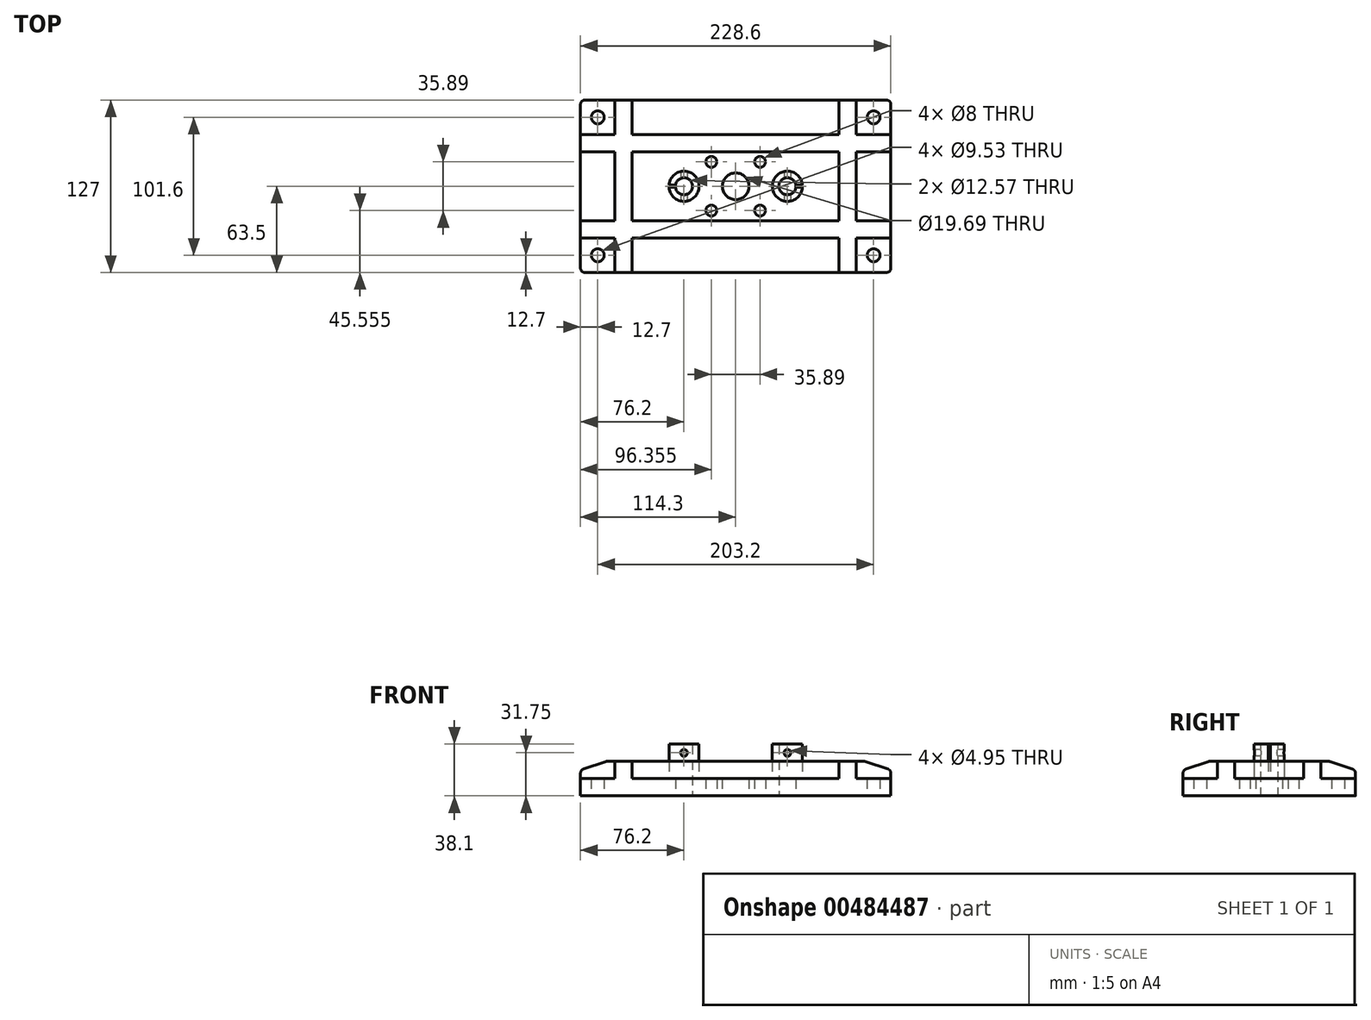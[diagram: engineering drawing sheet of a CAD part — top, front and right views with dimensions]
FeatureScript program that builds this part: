
annotation { "Feature Type Name" : "Feature", "Feature Type Description" : "" }
export const myFeature = defineFeature(function(context is Context, id is Id, definition is map)
    precondition{}
    {
        {
            var Q0;
            Q0=qCreatedBy(makeId("Top.planeOp"),FACE);
            var sketch = newSketch(context, id + "F0", { "sketchPlane" : qUnion([Q0])});
            skCircle(sketch, "E0", {"center": v(0, 0) * mm, "radius": 9.84 * mm});
            skCircle(sketch, "E1", {"center": v(38.1, 0) * mm, "radius": 6.29 * mm});
            skCircle(sketch, "E2", {"center": v(-38.1, 0) * mm, "radius": 6.29 * mm});
            skLineSegment(sketch, "E3", {"start": v(-38.1, 0) * mm, "end": v(0, 0) * mm, "construction": true});
            skLineSegment(sketch, "E4", {"start": v(38.1, 0) * mm, "end": v(0, 0) * mm, "construction": true});
            skLineSegment(sketch, "E5.bottom", {"start": v(-114.3, 63.5) * mm, "end": v(114.3, 63.5) * mm});
            skLineSegment(sketch, "E5.top", {"start": v(-114.3, -63.5) * mm, "end": v(114.3, -63.5) * mm});
            skLineSegment(sketch, "E5.left", {"start": v(-114.3, 63.5) * mm, "end": v(-114.3, -63.5) * mm});
            skLineSegment(sketch, "E5.right", {"start": v(114.3, 63.5) * mm, "end": v(114.3, -63.5) * mm});
            skLineSegment(sketch, "E6.bottom", {"start": v(17.95, 17.95) * mm, "end": v(-17.95, 17.95) * mm, "construction": true});
            skLineSegment(sketch, "E6.top", {"start": v(17.95, -17.95) * mm, "end": v(-17.95, -17.95) * mm, "construction": true});
            skLineSegment(sketch, "E6.left", {"start": v(17.95, 17.95) * mm, "end": v(17.95, -17.95) * mm, "construction": true});
            skLineSegment(sketch, "E6.right", {"start": v(-17.95, 17.95) * mm, "end": v(-17.95, -17.95) * mm, "construction": true});
            skCircle(sketch, "E7", {"center": v(-17.95, 17.95) * mm, "radius": 4 * mm});
            skCircle(sketch, "E8", {"center": v(17.95, 17.95) * mm, "radius": 4 * mm});
            skCircle(sketch, "E9", {"center": v(17.95, -17.95) * mm, "radius": 4 * mm});
            skCircle(sketch, "E10", {"center": v(-17.95, -17.95) * mm, "radius": 4 * mm});
            skLineSegment(sketch, "E11.bottom", {"start": v(-101.6, 50.8) * mm, "end": v(101.6, 50.8) * mm, "construction": true});
            skLineSegment(sketch, "E11.top", {"start": v(-101.6, -50.8) * mm, "end": v(101.6, -50.8) * mm, "construction": true});
            skLineSegment(sketch, "E11.left", {"start": v(-101.6, 50.8) * mm, "end": v(-101.6, -50.8) * mm, "construction": true});
            skLineSegment(sketch, "E11.right", {"start": v(101.6, 50.8) * mm, "end": v(101.6, -50.8) * mm, "construction": true});
            skCircle(sketch, "E12", {"center": v(-101.6, 50.8) * mm, "radius": 4.76 * mm});
            skCircle(sketch, "E13", {"center": v(101.6, 50.8) * mm, "radius": 4.76 * mm});
            skCircle(sketch, "E14", {"center": v(101.6, -50.8) * mm, "radius": 4.76 * mm});
            skCircle(sketch, "E15", {"center": v(-101.6, -50.8) * mm, "radius": 4.76 * mm});
            skSolve(sketch);
        }
        {
            var Q0;
            Q0 = qSketchRegion(id + "F0", true);
            extrude(context, id + "F1", {"entities" : qUnion([Q0]), "depth" : 12.7 * mm});
        }
        {
            var Q0;
            Q0=makeQuery(id+"F1.opExtrude","CAP_FACE",FACE,{"disambiguationData":[OSD([sQuery(id+"F0.wireOp",EDGE,"E0"),sQuery(id+"F0.wireOp",EDGE,"E1"),sQuery(id+"F0.wireOp",EDGE,"E2"),sQuery(id+"F0.wireOp",EDGE,"E5.bottom"),sQuery(id+"F0.wireOp",EDGE,"E5.top"),sQuery(id+"F0.wireOp",EDGE,"E5.left"),sQuery(id+"F0.wireOp",EDGE,"E5.right"),sQuery(id+"F0.wireOp",EDGE,"E7"),sQuery(id+"F0.wireOp",EDGE,"E8"),sQuery(id+"F0.wireOp",EDGE,"E9"),sQuery(id+"F0.wireOp",EDGE,"E10")])],"isStart":false});
            var sketch = newSketch(context, id + "F2", { "sketchPlane" : qUnion([Q0])});
            skCircle(sketch, "E16", {"center": v(-38.1, 0) * mm, "radius": 11.11 * mm});
            skCircle(sketch, "E17", {"center": v(38.1, 0) * mm, "radius": 11.11 * mm});
            skCircle(sketch, "E18.0", {"center": v(-38.1, 0) * mm, "radius": 6.29 * mm});
            skCircle(sketch, "E19.0", {"center": v(38.1, 0) * mm, "radius": 6.29 * mm});
            skSolve(sketch);
        }
        {
            var Q0;
            Q0 = qSketchRegion(id + "F2", true);
            extrude(context, id + "F3", {"entities" : qUnion([Q0]), "operationType" : NewBodyOperationType.ADD, "depth" : 25.4 * mm});
        }
        {
            var Q0;
            Q0=makeQuery(id+"F3.opExtrude","CAP_FACE",FACE,{"disambiguationData":[OSD([sQuery(id+"F2.wireOp",EDGE,"E16"),sQuery(id+"F2.wireOp",EDGE,"E18.0")])],"isStart":false});
            var sketch = newSketch(context, id + "F4", { "sketchPlane" : qUnion([Q0])});
            skLineSegment(sketch, "E20.bottom", {"start": v(-37.57, 0.8) * mm, "end": v(-60.85, 0.8) * mm});
            skLineSegment(sketch, "E20.top", {"start": v(-37.57, -0.8) * mm, "end": v(-60.85, -0.8) * mm});
            skLineSegment(sketch, "E20.left", {"start": v(-37.57, 0.8) * mm, "end": v(-37.57, -0.8) * mm});
            skLineSegment(sketch, "E20.right", {"start": v(-60.85, 0.8) * mm, "end": v(-60.85, -0.8) * mm});
            skPoint(sketch, "E20.middle", {"position": v(-49.21, 0) * mm});
            skLineSegment(sketch, "E21.bottom", {"start": v(42.1, 0.8) * mm, "end": v(65.37, 0.8) * mm});
            skLineSegment(sketch, "E21.top", {"start": v(42.1, -0.8) * mm, "end": v(65.37, -0.8) * mm});
            skLineSegment(sketch, "E21.left", {"start": v(42.1, 0.8) * mm, "end": v(42.1, -0.8) * mm});
            skLineSegment(sketch, "E21.right", {"start": v(65.37, 0.8) * mm, "end": v(65.37, -0.8) * mm});
            skPoint(sketch, "E21.middle", {"position": v(53.73, 0) * mm});
            skSolve(sketch);
        }
        {
            var Q0;
            Q0=makeQuery(id+"F4.imprint","IMPRINT",FACE,{"disambiguationData":[TD([[makeQuery(id+"F4.imprint","IMPRINT",EDGE,{"derivedFrom":sQuery(id+"F4.wireOp",EDGE,"E21.bottom")}),-1.0]])]});
            var Q1;
            {var subQ0=sQuery(id+"F4.wireOp",EDGE,"E20.left");Q1=makeQuery(id+"F4.imprint","IMPRINT",FACE,{"disambiguationData":[TD([[makeQuery(id+"F4.imprint","IMPRINT",EDGE,{"derivedFrom":subQ0}),-1.0]])]});}
            var Q2;
            {var subQ0=sQuery(id+"F4.wireOp",EDGE,"E20.bottom");var subQ1=makeQuery(id+"F3.opExtrude","CAP_EDGE",EDGE,{"disambiguationData":[OSD([sQuery(id+"F2.wireOp",EDGE,"E16")])],"isStart":false});var subQ2=makeQuery(id+"F4.imprint","INTERSECT",VERTEX,{"derivedFrom":[subQ1,subQ0]});Q2=makeQuery(id+"F4.imprint","IMPRINT",FACE,{"disambiguationData":[TD([[makeQuery(id+"F4.imprint","IMPRINT",EDGE,{"disambiguationData":[TD([[subQ2,1.0]])],"derivedFrom":subQ0}),1.0]])]});}
            var Q3;
            {var subQ0=sQuery(id+"F4.wireOp",EDGE,"E20.right");Q3=makeQuery(id+"F4.imprint","IMPRINT",FACE,{"disambiguationData":[TD([[makeQuery(id+"F4.imprint","IMPRINT",EDGE,{"derivedFrom":subQ0}),1.0]])]});}
            var Q4;
            Q4=makeQuery(id+"F1.opExtrude","CAP_FACE",FACE,{"disambiguationData":[OSD([sQuery(id+"F0.wireOp",EDGE,"E0"),sQuery(id+"F0.wireOp",EDGE,"E1"),sQuery(id+"F0.wireOp",EDGE,"E2"),sQuery(id+"F0.wireOp",EDGE,"E5.bottom"),sQuery(id+"F0.wireOp",EDGE,"E5.top"),sQuery(id+"F0.wireOp",EDGE,"E5.left"),sQuery(id+"F0.wireOp",EDGE,"E5.right"),sQuery(id+"F0.wireOp",EDGE,"E7"),sQuery(id+"F0.wireOp",EDGE,"E8"),sQuery(id+"F0.wireOp",EDGE,"E9"),sQuery(id+"F0.wireOp",EDGE,"E10"),sQuery(id+"F0.wireOp",EDGE,"E12"),sQuery(id+"F0.wireOp",EDGE,"E13"),sQuery(id+"F0.wireOp",EDGE,"E14"),sQuery(id+"F0.wireOp",EDGE,"E15")])],"isStart":false});
            extrude(context, id + "F5", {"entities" : qUnion([Q0, Q1, Q2, Q3]), "operationType" : NewBodyOperationType.REMOVE, "endBound" : BoundingType.UP_TO_SURFACE, "oppositeDirection" : true, "endBoundEntityFace" : qUnion([Q4]), "depth" : 25.4 * mm});
        }
        {
            var Q0;
            {var subQ0=sQuery(id+"F0.wireOp",EDGE,"E15");var subQ1=sQuery(id+"F0.wireOp",EDGE,"E14");var subQ2=sQuery(id+"F0.wireOp",EDGE,"E13");var subQ3=sQuery(id+"F0.wireOp",EDGE,"E12");var subQ4=sQuery(id+"F0.wireOp",EDGE,"E10");var subQ5=sQuery(id+"F0.wireOp",EDGE,"E9");var subQ6=sQuery(id+"F0.wireOp",EDGE,"E8");var subQ7=sQuery(id+"F0.wireOp",EDGE,"E7");var subQ8=sQuery(id+"F0.wireOp",EDGE,"E5.right");var subQ9=sQuery(id+"F0.wireOp",EDGE,"E5.left");var subQ10=sQuery(id+"F0.wireOp",EDGE,"E5.top");var subQ11=sQuery(id+"F0.wireOp",EDGE,"E5.bottom");var subQ12=sQuery(id+"F0.wireOp",EDGE,"E2");var subQ13=sQuery(id+"F0.wireOp",EDGE,"E1");var subQ14=sQuery(id+"F0.wireOp",EDGE,"E0");var subQ15=sQuery(id+"F4.wireOp",EDGE,"E20.bottom");Q0=makeQuery(id+"F5.boolean.opBoolean","MERGE",FACE,{"derivedFrom":[makeQuery(id+"F1.opExtrude","CAP_FACE",FACE,{"disambiguationData":[OSD([subQ14,subQ13,subQ12,subQ11,subQ10,subQ9,subQ8,subQ7,subQ6,subQ5,subQ4,subQ3,subQ2,subQ1,subQ0])],"isStart":false}),makeQuery(id+"F5.opExtrude","CAP_FACE",FACE,{"disambiguationData":[OSD([subQ14,subQ13,subQ12,subQ11,subQ10,subQ9,subQ8,subQ7,subQ6,subQ5,subQ4,subQ3,subQ2,subQ1,subQ0]),ownerDisambiguation([makeQuery(id+"F4.imprint","IMPRINT",EDGE,{"disambiguationData":[TD([[makeQuery(id+"F4.imprint","INTERSECT",VERTEX,{"derivedFrom":[subQ15,sQuery(id+"F4.wireOp",EDGE,"E20.left")]}),-1.0]])],"derivedFrom":subQ15})])],"isStart":false}),makeQuery(id+"F5.opExtrude","CAP_FACE",FACE,{"disambiguationData":[OSD([subQ14,subQ13,subQ12,subQ11,subQ10,subQ9,subQ8,subQ7,subQ6,subQ5,subQ4,subQ3,subQ2,subQ1,subQ0]),ownerDisambiguation([makeQuery(id+"F4.imprint","IMPRINT",EDGE,{"derivedFrom":sQuery(id+"F4.wireOp",EDGE,"E21.bottom")})])],"isStart":false})]});}
            var sketch = newSketch(context, id + "F6", { "sketchPlane" : qUnion([Q0])});
            skLineSegment(sketch, "E22.bottom", {"start": v(-88.9, 63.5) * mm, "end": v(-76.2, 63.5) * mm});
            skLineSegment(sketch, "E22.top", {"start": v(-88.9, -63.5) * mm, "end": v(-76.2, -63.5) * mm});
            skLineSegment(sketch, "E22.left", {"start": v(-88.9, 63.5) * mm, "end": v(-88.9, -63.5) * mm});
            skLineSegment(sketch, "E22.right", {"start": v(-76.2, 63.5) * mm, "end": v(-76.2, -63.5) * mm});
            skLineSegment(sketch, "E23.bottom", {"start": v(88.9, 63.5) * mm, "end": v(76.2, 63.5) * mm});
            skLineSegment(sketch, "E23.top", {"start": v(88.9, -63.5) * mm, "end": v(76.2, -63.5) * mm});
            skLineSegment(sketch, "E23.left", {"start": v(88.9, 63.5) * mm, "end": v(88.9, -63.5) * mm});
            skLineSegment(sketch, "E23.right", {"start": v(76.2, 63.5) * mm, "end": v(76.2, -63.5) * mm});
            skLineSegment(sketch, "E24", {"start": v(-76.2, 0) * mm, "end": v(76.2, 0) * mm, "construction": true});
            skSolve(sketch);
        }
        {
            var Q0;
            Q0 = qSketchRegion(id + "F6", true);
            extrude(context, id + "F7", {"entities" : qUnion([Q0]), "operationType" : NewBodyOperationType.ADD, "depth" : 12.7 * mm});
        }
        {
            var Q0;
            {var subQ0=sQuery(id+"F0.wireOp",EDGE,"E1");var subQ1=sQuery(id+"F0.wireOp",EDGE,"E5.bottom");var subQ2=sQuery(id+"F0.wireOp",EDGE,"E0");var subQ3=sQuery(id+"F0.wireOp",EDGE,"E9");var subQ4=sQuery(id+"F4.wireOp",EDGE,"E21.bottom");var subQ5=sQuery(id+"F0.wireOp",EDGE,"E5.top");var subQ6=sQuery(id+"F0.wireOp",EDGE,"E7");var subQ8=sQuery(id+"F0.wireOp",EDGE,"E8");var subQ9=sQuery(id+"F0.wireOp",EDGE,"E10");var subQ10=sQuery(id+"F4.wireOp",EDGE,"E20.bottom");var subQ11=sQuery(id+"F0.wireOp",EDGE,"E2");var subQ12=sQuery(id+"F0.wireOp",EDGE,"E15");var subQ13=sQuery(id+"F0.wireOp",EDGE,"E14");var subQ14=sQuery(id+"F0.wireOp",EDGE,"E13");var subQ15=sQuery(id+"F0.wireOp",EDGE,"E12");var subQ16=sQuery(id+"F0.wireOp",EDGE,"E5.right");var subQ17=sQuery(id+"F0.wireOp",EDGE,"E5.left");Q0=makeQuery(id+"F7.boolean.opBoolean","SPLIT",FACE,{"disambiguationData":[TD([makeQuery(id+"F1.opExtrude","SWEPT_FACE",FACE,{"disambiguationData":[OSD([subQ2])]})])],"derivedFrom":makeQuery(id+"F5.boolean.opBoolean","MERGE",FACE,{"derivedFrom":[makeQuery(id+"F1.opExtrude","CAP_FACE",FACE,{"disambiguationData":[OSD([subQ2,subQ0,subQ11,subQ1,subQ5,subQ17,subQ16,subQ6,subQ8,subQ3,subQ9,subQ15,subQ14,subQ13,subQ12])],"isStart":false}),makeQuery(id+"F5.opExtrude","CAP_FACE",FACE,{"disambiguationData":[OSD([subQ2,subQ0,subQ11,subQ1,subQ5,subQ17,subQ16,subQ6,subQ8,subQ3,subQ9,subQ15,subQ14,subQ13,subQ12]),ownerDisambiguation([makeQuery(id+"F4.imprint","IMPRINT",EDGE,{"disambiguationData":[TD([[makeQuery(id+"F4.imprint","INTERSECT",VERTEX,{"derivedFrom":[subQ10,sQuery(id+"F4.wireOp",EDGE,"E20.left")]}),-1.0]])],"derivedFrom":subQ10})])],"isStart":false}),makeQuery(id+"F5.opExtrude","CAP_FACE",FACE,{"disambiguationData":[OSD([subQ2,subQ0,subQ11,subQ1,subQ5,subQ17,subQ16,subQ6,subQ8,subQ3,subQ9,subQ15,subQ14,subQ13,subQ12]),ownerDisambiguation([makeQuery(id+"F4.imprint","IMPRINT",EDGE,{"derivedFrom":subQ4})])],"isStart":false})]})});}
            var sketch = newSketch(context, id + "F8", { "sketchPlane" : qUnion([Q0])});
            skLineSegment(sketch, "E25.bottom", {"start": v(-114.3, -25.4) * mm, "end": v(114.3, -25.4) * mm});
            skLineSegment(sketch, "E25.top", {"start": v(-114.3, -38.1) * mm, "end": v(114.3, -38.1) * mm});
            skLineSegment(sketch, "E25.left", {"start": v(-114.3, -38.1) * mm, "end": v(-114.3, -25.4) * mm});
            skLineSegment(sketch, "E25.right", {"start": v(114.3, -38.1) * mm, "end": v(114.3, -25.4) * mm});
            skLineSegment(sketch, "E26.bottom", {"start": v(114.3, 38.1) * mm, "end": v(-114.3, 38.1) * mm});
            skLineSegment(sketch, "E26.top", {"start": v(114.3, 25.4) * mm, "end": v(-114.3, 25.4) * mm});
            skLineSegment(sketch, "E26.left", {"start": v(114.3, 38.1) * mm, "end": v(114.3, 25.4) * mm});
            skLineSegment(sketch, "E26.right", {"start": v(-114.3, 38.1) * mm, "end": v(-114.3, 25.4) * mm});
            skLineSegment(sketch, "E27", {"start": v(0, 25.4) * mm, "end": v(0, -25.4) * mm, "construction": true});
            skSolve(sketch);
        }
        {
            var Q0;
            Q0 = qSketchRegion(id + "F8", true);
            extrude(context, id + "F9", {"entities" : qUnion([Q0]), "operationType" : NewBodyOperationType.ADD, "depth" : 12.7 * mm});
        }
        {
            var Q0;
            Q0=makeQuery(id+"F1.opExtrude","SWEPT_EDGE",EDGE,{"disambiguationData":[OSD([sQuery(id+"F0.wireOp",EDGE,"E5.top"),sQuery(id+"F0.wireOp",EDGE,"E5.left")])]});
            var Q1;
            Q1=makeQuery(id+"F1.opExtrude","SWEPT_EDGE",EDGE,{"disambiguationData":[OSD([sQuery(id+"F0.wireOp",EDGE,"E5.top"),sQuery(id+"F0.wireOp",EDGE,"E5.right")])]});
            var Q2;
            Q2=makeQuery(id+"F1.opExtrude","SWEPT_EDGE",EDGE,{"disambiguationData":[OSD([sQuery(id+"F0.wireOp",EDGE,"E5.bottom"),sQuery(id+"F0.wireOp",EDGE,"E5.left")])]});
            var Q3;
            Q3=makeQuery(id+"F1.opExtrude","SWEPT_EDGE",EDGE,{"disambiguationData":[OSD([sQuery(id+"F0.wireOp",EDGE,"E5.bottom"),sQuery(id+"F0.wireOp",EDGE,"E5.right")])]});
            fillet(context, id + "F10", {"entities" : qUnion([Q0, Q1, Q2, Q3]), "radius" : 3.17 * mm, "tangentPropagation" : true, "allowEdgeOverflow" : false});
        }
        {
            var Q0;
            Q0=makeQuery(id+"F9.opExtrude","CAP_EDGE",EDGE,{"disambiguationData":[OSD([sQuery(id+"F8.wireOp",EDGE,"E26.right")])],"isStart":false});
            var Q1;
            Q1=makeQuery(id+"F9.opExtrude","CAP_EDGE",EDGE,{"disambiguationData":[OSD([sQuery(id+"F8.wireOp",EDGE,"E25.left")])],"isStart":false});
            var Q2;
            Q2=makeQuery(id+"F9.opExtrude","CAP_EDGE",EDGE,{"disambiguationData":[OSD([sQuery(id+"F8.wireOp",EDGE,"E25.right")])],"isStart":false});
            var Q3;
            Q3=makeQuery(id+"F9.opExtrude","CAP_EDGE",EDGE,{"disambiguationData":[OSD([sQuery(id+"F8.wireOp",EDGE,"E26.left")])],"isStart":false});
            var Q4;
            Q4=makeQuery(id+"F7.opExtrude","CAP_EDGE",EDGE,{"disambiguationData":[OSD([sQuery(id+"F6.wireOp",EDGE,"E22.top")])],"isStart":false});
            var Q5;
            Q5=makeQuery(id+"F7.opExtrude","CAP_EDGE",EDGE,{"disambiguationData":[OSD([sQuery(id+"F6.wireOp",EDGE,"E23.top")])],"isStart":false});
            var Q6;
            Q6=makeQuery(id+"F7.opExtrude","CAP_EDGE",EDGE,{"disambiguationData":[OSD([sQuery(id+"F6.wireOp",EDGE,"E23.bottom")])],"isStart":false});
            var Q7;
            Q7=makeQuery(id+"F7.opExtrude","CAP_EDGE",EDGE,{"disambiguationData":[OSD([sQuery(id+"F6.wireOp",EDGE,"E22.bottom")])],"isStart":false});
            chamfer(context, id + "F11", {"entities" : qUnion([Q0, Q1, Q2, Q3, Q4, Q5, Q6, Q7]), "chamferType" : ChamferType.TWO_OFFSETS, "width1" : 19.05 * mm, "oppositeDirection" : false, "width2" : 6.35 * mm, "tangentPropagation" : true});
        }
        {
            var Q0;
            {var subQ0=sQuery(id+"F8.wireOp",EDGE,"E25.left");Q0=makeQuery(id+"F11.opChamfer","BLEND_EDGE",EDGE,{"blendedFrom":[makeQuery(id+"F9.opExtrude","CAP_EDGE",EDGE,{"disambiguationData":[OSD([subQ0])],"isStart":false}),makeQuery(id+"F9.boolean.opBoolean","MERGE",FACE,{"derivedFrom":[makeQuery(id+"F1.opExtrude","SWEPT_FACE",FACE,{"disambiguationData":[OSD([sQuery(id+"F0.wireOp",EDGE,"E5.left")])]}),makeQuery(id+"F9.opExtrude","SWEPT_FACE",FACE,{"disambiguationData":[OSD([subQ0])]}),makeQuery(id+"F9.opExtrude","SWEPT_FACE",FACE,{"disambiguationData":[OSD([sQuery(id+"F8.wireOp",EDGE,"E26.right")])]})]})],"blendedInto":[makeQuery(id+"F9.boolean.opBoolean","MERGE",FACE,{"derivedFrom":[makeQuery(id+"F1.opExtrude","SWEPT_FACE",FACE,{"disambiguationData":[OSD([sQuery(id+"F0.wireOp",EDGE,"E5.left")])]}),makeQuery(id+"F9.opExtrude","SWEPT_FACE",FACE,{"disambiguationData":[OSD([subQ0])]}),makeQuery(id+"F9.opExtrude","SWEPT_FACE",FACE,{"disambiguationData":[OSD([sQuery(id+"F8.wireOp",EDGE,"E26.right")])]})]})]});}
            var Q1;
            {var subQ0=sQuery(id+"F8.wireOp",EDGE,"E26.right");Q1=makeQuery(id+"F11.opChamfer","BLEND_EDGE",EDGE,{"blendedFrom":[makeQuery(id+"F9.opExtrude","CAP_EDGE",EDGE,{"disambiguationData":[OSD([subQ0])],"isStart":false}),makeQuery(id+"F9.boolean.opBoolean","MERGE",FACE,{"derivedFrom":[makeQuery(id+"F1.opExtrude","SWEPT_FACE",FACE,{"disambiguationData":[OSD([sQuery(id+"F0.wireOp",EDGE,"E5.left")])]}),makeQuery(id+"F9.opExtrude","SWEPT_FACE",FACE,{"disambiguationData":[OSD([sQuery(id+"F8.wireOp",EDGE,"E25.left")])]}),makeQuery(id+"F9.opExtrude","SWEPT_FACE",FACE,{"disambiguationData":[OSD([subQ0])]})]})],"blendedInto":[makeQuery(id+"F9.boolean.opBoolean","MERGE",FACE,{"derivedFrom":[makeQuery(id+"F1.opExtrude","SWEPT_FACE",FACE,{"disambiguationData":[OSD([sQuery(id+"F0.wireOp",EDGE,"E5.left")])]}),makeQuery(id+"F9.opExtrude","SWEPT_FACE",FACE,{"disambiguationData":[OSD([sQuery(id+"F8.wireOp",EDGE,"E25.left")])]}),makeQuery(id+"F9.opExtrude","SWEPT_FACE",FACE,{"disambiguationData":[OSD([subQ0])]})]})]});}
            var Q2;
            {var subQ0=sQuery(id+"F8.wireOp",EDGE,"E26.right");Q2=makeQuery(id+"F11.opChamfer","BLEND_EDGE",EDGE,{"blendedFrom":[makeQuery(id+"F9.opExtrude","CAP_EDGE",EDGE,{"disambiguationData":[OSD([subQ0])],"isStart":false}),makeQuery(id+"F9.boolean.opBoolean","MERGE",FACE,{"derivedFrom":[makeQuery(id+"F7.opExtrude","CAP_FACE",FACE,{"disambiguationData":[OSD([sQuery(id+"F6.wireOp",EDGE,"E22.bottom"),sQuery(id+"F6.wireOp",EDGE,"E22.top"),sQuery(id+"F6.wireOp",EDGE,"E22.left"),sQuery(id+"F6.wireOp",EDGE,"E22.right")])],"isStart":false}),makeQuery(id+"F7.opExtrude","CAP_FACE",FACE,{"disambiguationData":[OSD([sQuery(id+"F6.wireOp",EDGE,"E23.bottom"),sQuery(id+"F6.wireOp",EDGE,"E23.top"),sQuery(id+"F6.wireOp",EDGE,"E23.left"),sQuery(id+"F6.wireOp",EDGE,"E23.right")])],"isStart":false}),makeQuery(id+"F9.opExtrude","CAP_FACE",FACE,{"disambiguationData":[OSD([sQuery(id+"F8.wireOp",EDGE,"E25.bottom"),sQuery(id+"F8.wireOp",EDGE,"E25.top"),sQuery(id+"F8.wireOp",EDGE,"E25.left"),sQuery(id+"F8.wireOp",EDGE,"E25.right")])],"isStart":false}),makeQuery(id+"F9.opExtrude","CAP_FACE",FACE,{"disambiguationData":[OSD([sQuery(id+"F8.wireOp",EDGE,"E26.bottom"),sQuery(id+"F8.wireOp",EDGE,"E26.top"),sQuery(id+"F8.wireOp",EDGE,"E26.left"),subQ0])],"isStart":false})]})],"blendedInto":[makeQuery(id+"F9.boolean.opBoolean","MERGE",FACE,{"derivedFrom":[makeQuery(id+"F7.opExtrude","CAP_FACE",FACE,{"disambiguationData":[OSD([sQuery(id+"F6.wireOp",EDGE,"E22.bottom"),sQuery(id+"F6.wireOp",EDGE,"E22.top"),sQuery(id+"F6.wireOp",EDGE,"E22.left"),sQuery(id+"F6.wireOp",EDGE,"E22.right")])],"isStart":false}),makeQuery(id+"F7.opExtrude","CAP_FACE",FACE,{"disambiguationData":[OSD([sQuery(id+"F6.wireOp",EDGE,"E23.bottom"),sQuery(id+"F6.wireOp",EDGE,"E23.top"),sQuery(id+"F6.wireOp",EDGE,"E23.left"),sQuery(id+"F6.wireOp",EDGE,"E23.right")])],"isStart":false}),makeQuery(id+"F9.opExtrude","CAP_FACE",FACE,{"disambiguationData":[OSD([sQuery(id+"F8.wireOp",EDGE,"E25.bottom"),sQuery(id+"F8.wireOp",EDGE,"E25.top"),sQuery(id+"F8.wireOp",EDGE,"E25.left"),sQuery(id+"F8.wireOp",EDGE,"E25.right")])],"isStart":false}),makeQuery(id+"F9.opExtrude","CAP_FACE",FACE,{"disambiguationData":[OSD([sQuery(id+"F8.wireOp",EDGE,"E26.bottom"),sQuery(id+"F8.wireOp",EDGE,"E26.top"),sQuery(id+"F8.wireOp",EDGE,"E26.left"),subQ0])],"isStart":false})]})]});}
            var Q3;
            {var subQ0=sQuery(id+"F8.wireOp",EDGE,"E25.left");Q3=makeQuery(id+"F11.opChamfer","BLEND_EDGE",EDGE,{"blendedFrom":[makeQuery(id+"F9.opExtrude","CAP_EDGE",EDGE,{"disambiguationData":[OSD([subQ0])],"isStart":false}),makeQuery(id+"F9.boolean.opBoolean","MERGE",FACE,{"derivedFrom":[makeQuery(id+"F7.opExtrude","CAP_FACE",FACE,{"disambiguationData":[OSD([sQuery(id+"F6.wireOp",EDGE,"E22.bottom"),sQuery(id+"F6.wireOp",EDGE,"E22.top"),sQuery(id+"F6.wireOp",EDGE,"E22.left"),sQuery(id+"F6.wireOp",EDGE,"E22.right")])],"isStart":false}),makeQuery(id+"F7.opExtrude","CAP_FACE",FACE,{"disambiguationData":[OSD([sQuery(id+"F6.wireOp",EDGE,"E23.bottom"),sQuery(id+"F6.wireOp",EDGE,"E23.top"),sQuery(id+"F6.wireOp",EDGE,"E23.left"),sQuery(id+"F6.wireOp",EDGE,"E23.right")])],"isStart":false}),makeQuery(id+"F9.opExtrude","CAP_FACE",FACE,{"disambiguationData":[OSD([sQuery(id+"F8.wireOp",EDGE,"E25.bottom"),sQuery(id+"F8.wireOp",EDGE,"E25.top"),subQ0,sQuery(id+"F8.wireOp",EDGE,"E25.right")])],"isStart":false}),makeQuery(id+"F9.opExtrude","CAP_FACE",FACE,{"disambiguationData":[OSD([sQuery(id+"F8.wireOp",EDGE,"E26.bottom"),sQuery(id+"F8.wireOp",EDGE,"E26.top"),sQuery(id+"F8.wireOp",EDGE,"E26.left"),sQuery(id+"F8.wireOp",EDGE,"E26.right")])],"isStart":false})]})],"blendedInto":[makeQuery(id+"F9.boolean.opBoolean","MERGE",FACE,{"derivedFrom":[makeQuery(id+"F7.opExtrude","CAP_FACE",FACE,{"disambiguationData":[OSD([sQuery(id+"F6.wireOp",EDGE,"E22.bottom"),sQuery(id+"F6.wireOp",EDGE,"E22.top"),sQuery(id+"F6.wireOp",EDGE,"E22.left"),sQuery(id+"F6.wireOp",EDGE,"E22.right")])],"isStart":false}),makeQuery(id+"F7.opExtrude","CAP_FACE",FACE,{"disambiguationData":[OSD([sQuery(id+"F6.wireOp",EDGE,"E23.bottom"),sQuery(id+"F6.wireOp",EDGE,"E23.top"),sQuery(id+"F6.wireOp",EDGE,"E23.left"),sQuery(id+"F6.wireOp",EDGE,"E23.right")])],"isStart":false}),makeQuery(id+"F9.opExtrude","CAP_FACE",FACE,{"disambiguationData":[OSD([sQuery(id+"F8.wireOp",EDGE,"E25.bottom"),sQuery(id+"F8.wireOp",EDGE,"E25.top"),subQ0,sQuery(id+"F8.wireOp",EDGE,"E25.right")])],"isStart":false}),makeQuery(id+"F9.opExtrude","CAP_FACE",FACE,{"disambiguationData":[OSD([sQuery(id+"F8.wireOp",EDGE,"E26.bottom"),sQuery(id+"F8.wireOp",EDGE,"E26.top"),sQuery(id+"F8.wireOp",EDGE,"E26.left"),sQuery(id+"F8.wireOp",EDGE,"E26.right")])],"isStart":false})]})]});}
            var Q4;
            {var subQ0=sQuery(id+"F8.wireOp",EDGE,"E25.right");Q4=makeQuery(id+"F11.opChamfer","BLEND_EDGE",EDGE,{"blendedFrom":[makeQuery(id+"F9.opExtrude","CAP_EDGE",EDGE,{"disambiguationData":[OSD([subQ0])],"isStart":false}),makeQuery(id+"F9.boolean.opBoolean","MERGE",FACE,{"derivedFrom":[makeQuery(id+"F7.opExtrude","CAP_FACE",FACE,{"disambiguationData":[OSD([sQuery(id+"F6.wireOp",EDGE,"E22.bottom"),sQuery(id+"F6.wireOp",EDGE,"E22.top"),sQuery(id+"F6.wireOp",EDGE,"E22.left"),sQuery(id+"F6.wireOp",EDGE,"E22.right")])],"isStart":false}),makeQuery(id+"F7.opExtrude","CAP_FACE",FACE,{"disambiguationData":[OSD([sQuery(id+"F6.wireOp",EDGE,"E23.bottom"),sQuery(id+"F6.wireOp",EDGE,"E23.top"),sQuery(id+"F6.wireOp",EDGE,"E23.left"),sQuery(id+"F6.wireOp",EDGE,"E23.right")])],"isStart":false}),makeQuery(id+"F9.opExtrude","CAP_FACE",FACE,{"disambiguationData":[OSD([sQuery(id+"F8.wireOp",EDGE,"E25.bottom"),sQuery(id+"F8.wireOp",EDGE,"E25.top"),sQuery(id+"F8.wireOp",EDGE,"E25.left"),subQ0])],"isStart":false}),makeQuery(id+"F9.opExtrude","CAP_FACE",FACE,{"disambiguationData":[OSD([sQuery(id+"F8.wireOp",EDGE,"E26.bottom"),sQuery(id+"F8.wireOp",EDGE,"E26.top"),sQuery(id+"F8.wireOp",EDGE,"E26.left"),sQuery(id+"F8.wireOp",EDGE,"E26.right")])],"isStart":false})]})],"blendedInto":[makeQuery(id+"F9.boolean.opBoolean","MERGE",FACE,{"derivedFrom":[makeQuery(id+"F7.opExtrude","CAP_FACE",FACE,{"disambiguationData":[OSD([sQuery(id+"F6.wireOp",EDGE,"E22.bottom"),sQuery(id+"F6.wireOp",EDGE,"E22.top"),sQuery(id+"F6.wireOp",EDGE,"E22.left"),sQuery(id+"F6.wireOp",EDGE,"E22.right")])],"isStart":false}),makeQuery(id+"F7.opExtrude","CAP_FACE",FACE,{"disambiguationData":[OSD([sQuery(id+"F6.wireOp",EDGE,"E23.bottom"),sQuery(id+"F6.wireOp",EDGE,"E23.top"),sQuery(id+"F6.wireOp",EDGE,"E23.left"),sQuery(id+"F6.wireOp",EDGE,"E23.right")])],"isStart":false}),makeQuery(id+"F9.opExtrude","CAP_FACE",FACE,{"disambiguationData":[OSD([sQuery(id+"F8.wireOp",EDGE,"E25.bottom"),sQuery(id+"F8.wireOp",EDGE,"E25.top"),sQuery(id+"F8.wireOp",EDGE,"E25.left"),subQ0])],"isStart":false}),makeQuery(id+"F9.opExtrude","CAP_FACE",FACE,{"disambiguationData":[OSD([sQuery(id+"F8.wireOp",EDGE,"E26.bottom"),sQuery(id+"F8.wireOp",EDGE,"E26.top"),sQuery(id+"F8.wireOp",EDGE,"E26.left"),sQuery(id+"F8.wireOp",EDGE,"E26.right")])],"isStart":false})]})]});}
            var Q5;
            {var subQ0=sQuery(id+"F8.wireOp",EDGE,"E25.right");Q5=makeQuery(id+"F11.opChamfer","BLEND_EDGE",EDGE,{"blendedFrom":[makeQuery(id+"F9.opExtrude","CAP_EDGE",EDGE,{"disambiguationData":[OSD([subQ0])],"isStart":false}),makeQuery(id+"F9.boolean.opBoolean","MERGE",FACE,{"derivedFrom":[makeQuery(id+"F1.opExtrude","SWEPT_FACE",FACE,{"disambiguationData":[OSD([sQuery(id+"F0.wireOp",EDGE,"E5.right")])]}),makeQuery(id+"F9.opExtrude","SWEPT_FACE",FACE,{"disambiguationData":[OSD([subQ0])]}),makeQuery(id+"F9.opExtrude","SWEPT_FACE",FACE,{"disambiguationData":[OSD([sQuery(id+"F8.wireOp",EDGE,"E26.left")])]})]})],"blendedInto":[makeQuery(id+"F9.boolean.opBoolean","MERGE",FACE,{"derivedFrom":[makeQuery(id+"F1.opExtrude","SWEPT_FACE",FACE,{"disambiguationData":[OSD([sQuery(id+"F0.wireOp",EDGE,"E5.right")])]}),makeQuery(id+"F9.opExtrude","SWEPT_FACE",FACE,{"disambiguationData":[OSD([subQ0])]}),makeQuery(id+"F9.opExtrude","SWEPT_FACE",FACE,{"disambiguationData":[OSD([sQuery(id+"F8.wireOp",EDGE,"E26.left")])]})]})]});}
            var Q6;
            {var subQ0=sQuery(id+"F8.wireOp",EDGE,"E26.left");Q6=makeQuery(id+"F11.opChamfer","BLEND_EDGE",EDGE,{"blendedFrom":[makeQuery(id+"F9.opExtrude","CAP_EDGE",EDGE,{"disambiguationData":[OSD([subQ0])],"isStart":false}),makeQuery(id+"F9.boolean.opBoolean","MERGE",FACE,{"derivedFrom":[makeQuery(id+"F1.opExtrude","SWEPT_FACE",FACE,{"disambiguationData":[OSD([sQuery(id+"F0.wireOp",EDGE,"E5.right")])]}),makeQuery(id+"F9.opExtrude","SWEPT_FACE",FACE,{"disambiguationData":[OSD([sQuery(id+"F8.wireOp",EDGE,"E25.right")])]}),makeQuery(id+"F9.opExtrude","SWEPT_FACE",FACE,{"disambiguationData":[OSD([subQ0])]})]})],"blendedInto":[makeQuery(id+"F9.boolean.opBoolean","MERGE",FACE,{"derivedFrom":[makeQuery(id+"F1.opExtrude","SWEPT_FACE",FACE,{"disambiguationData":[OSD([sQuery(id+"F0.wireOp",EDGE,"E5.right")])]}),makeQuery(id+"F9.opExtrude","SWEPT_FACE",FACE,{"disambiguationData":[OSD([sQuery(id+"F8.wireOp",EDGE,"E25.right")])]}),makeQuery(id+"F9.opExtrude","SWEPT_FACE",FACE,{"disambiguationData":[OSD([subQ0])]})]})]});}
            var Q7;
            {var subQ0=sQuery(id+"F8.wireOp",EDGE,"E26.left");Q7=makeQuery(id+"F11.opChamfer","BLEND_EDGE",EDGE,{"blendedFrom":[makeQuery(id+"F9.opExtrude","CAP_EDGE",EDGE,{"disambiguationData":[OSD([subQ0])],"isStart":false}),makeQuery(id+"F9.boolean.opBoolean","MERGE",FACE,{"derivedFrom":[makeQuery(id+"F7.opExtrude","CAP_FACE",FACE,{"disambiguationData":[OSD([sQuery(id+"F6.wireOp",EDGE,"E22.bottom"),sQuery(id+"F6.wireOp",EDGE,"E22.top"),sQuery(id+"F6.wireOp",EDGE,"E22.left"),sQuery(id+"F6.wireOp",EDGE,"E22.right")])],"isStart":false}),makeQuery(id+"F7.opExtrude","CAP_FACE",FACE,{"disambiguationData":[OSD([sQuery(id+"F6.wireOp",EDGE,"E23.bottom"),sQuery(id+"F6.wireOp",EDGE,"E23.top"),sQuery(id+"F6.wireOp",EDGE,"E23.left"),sQuery(id+"F6.wireOp",EDGE,"E23.right")])],"isStart":false}),makeQuery(id+"F9.opExtrude","CAP_FACE",FACE,{"disambiguationData":[OSD([sQuery(id+"F8.wireOp",EDGE,"E25.bottom"),sQuery(id+"F8.wireOp",EDGE,"E25.top"),sQuery(id+"F8.wireOp",EDGE,"E25.left"),sQuery(id+"F8.wireOp",EDGE,"E25.right")])],"isStart":false}),makeQuery(id+"F9.opExtrude","CAP_FACE",FACE,{"disambiguationData":[OSD([sQuery(id+"F8.wireOp",EDGE,"E26.bottom"),sQuery(id+"F8.wireOp",EDGE,"E26.top"),subQ0,sQuery(id+"F8.wireOp",EDGE,"E26.right")])],"isStart":false})]})],"blendedInto":[makeQuery(id+"F9.boolean.opBoolean","MERGE",FACE,{"derivedFrom":[makeQuery(id+"F7.opExtrude","CAP_FACE",FACE,{"disambiguationData":[OSD([sQuery(id+"F6.wireOp",EDGE,"E22.bottom"),sQuery(id+"F6.wireOp",EDGE,"E22.top"),sQuery(id+"F6.wireOp",EDGE,"E22.left"),sQuery(id+"F6.wireOp",EDGE,"E22.right")])],"isStart":false}),makeQuery(id+"F7.opExtrude","CAP_FACE",FACE,{"disambiguationData":[OSD([sQuery(id+"F6.wireOp",EDGE,"E23.bottom"),sQuery(id+"F6.wireOp",EDGE,"E23.top"),sQuery(id+"F6.wireOp",EDGE,"E23.left"),sQuery(id+"F6.wireOp",EDGE,"E23.right")])],"isStart":false}),makeQuery(id+"F9.opExtrude","CAP_FACE",FACE,{"disambiguationData":[OSD([sQuery(id+"F8.wireOp",EDGE,"E25.bottom"),sQuery(id+"F8.wireOp",EDGE,"E25.top"),sQuery(id+"F8.wireOp",EDGE,"E25.left"),sQuery(id+"F8.wireOp",EDGE,"E25.right")])],"isStart":false}),makeQuery(id+"F9.opExtrude","CAP_FACE",FACE,{"disambiguationData":[OSD([sQuery(id+"F8.wireOp",EDGE,"E26.bottom"),sQuery(id+"F8.wireOp",EDGE,"E26.top"),subQ0,sQuery(id+"F8.wireOp",EDGE,"E26.right")])],"isStart":false})]})]});}
            var Q8;
            {var subQ0=sQuery(id+"F6.wireOp",EDGE,"E22.top");Q8=makeQuery(id+"F11.opChamfer","BLEND_EDGE",EDGE,{"blendedFrom":[makeQuery(id+"F7.opExtrude","CAP_EDGE",EDGE,{"disambiguationData":[OSD([subQ0])],"isStart":false}),makeQuery(id+"F7.boolean.opBoolean","MERGE",FACE,{"derivedFrom":[makeQuery(id+"F1.opExtrude","SWEPT_FACE",FACE,{"disambiguationData":[OSD([sQuery(id+"F0.wireOp",EDGE,"E5.top")])]}),makeQuery(id+"F7.opExtrude","SWEPT_FACE",FACE,{"disambiguationData":[OSD([subQ0])]}),makeQuery(id+"F7.opExtrude","SWEPT_FACE",FACE,{"disambiguationData":[OSD([sQuery(id+"F6.wireOp",EDGE,"E23.top")])]})]})],"blendedInto":[makeQuery(id+"F7.boolean.opBoolean","MERGE",FACE,{"derivedFrom":[makeQuery(id+"F1.opExtrude","SWEPT_FACE",FACE,{"disambiguationData":[OSD([sQuery(id+"F0.wireOp",EDGE,"E5.top")])]}),makeQuery(id+"F7.opExtrude","SWEPT_FACE",FACE,{"disambiguationData":[OSD([subQ0])]}),makeQuery(id+"F7.opExtrude","SWEPT_FACE",FACE,{"disambiguationData":[OSD([sQuery(id+"F6.wireOp",EDGE,"E23.top")])]})]})]});}
            var Q9;
            {var subQ0=sQuery(id+"F6.wireOp",EDGE,"E23.top");Q9=makeQuery(id+"F11.opChamfer","BLEND_EDGE",EDGE,{"blendedFrom":[makeQuery(id+"F7.opExtrude","CAP_EDGE",EDGE,{"disambiguationData":[OSD([subQ0])],"isStart":false}),makeQuery(id+"F7.boolean.opBoolean","MERGE",FACE,{"derivedFrom":[makeQuery(id+"F1.opExtrude","SWEPT_FACE",FACE,{"disambiguationData":[OSD([sQuery(id+"F0.wireOp",EDGE,"E5.top")])]}),makeQuery(id+"F7.opExtrude","SWEPT_FACE",FACE,{"disambiguationData":[OSD([sQuery(id+"F6.wireOp",EDGE,"E22.top")])]}),makeQuery(id+"F7.opExtrude","SWEPT_FACE",FACE,{"disambiguationData":[OSD([subQ0])]})]})],"blendedInto":[makeQuery(id+"F7.boolean.opBoolean","MERGE",FACE,{"derivedFrom":[makeQuery(id+"F1.opExtrude","SWEPT_FACE",FACE,{"disambiguationData":[OSD([sQuery(id+"F0.wireOp",EDGE,"E5.top")])]}),makeQuery(id+"F7.opExtrude","SWEPT_FACE",FACE,{"disambiguationData":[OSD([sQuery(id+"F6.wireOp",EDGE,"E22.top")])]}),makeQuery(id+"F7.opExtrude","SWEPT_FACE",FACE,{"disambiguationData":[OSD([subQ0])]})]})]});}
            var Q10;
            {var subQ0=sQuery(id+"F6.wireOp",EDGE,"E23.top");Q10=makeQuery(id+"F11.opChamfer","BLEND_EDGE",EDGE,{"blendedFrom":[makeQuery(id+"F7.opExtrude","CAP_EDGE",EDGE,{"disambiguationData":[OSD([subQ0])],"isStart":false}),makeQuery(id+"F9.boolean.opBoolean","MERGE",FACE,{"derivedFrom":[makeQuery(id+"F7.opExtrude","CAP_FACE",FACE,{"disambiguationData":[OSD([sQuery(id+"F6.wireOp",EDGE,"E22.bottom"),sQuery(id+"F6.wireOp",EDGE,"E22.top"),sQuery(id+"F6.wireOp",EDGE,"E22.left"),sQuery(id+"F6.wireOp",EDGE,"E22.right")])],"isStart":false}),makeQuery(id+"F7.opExtrude","CAP_FACE",FACE,{"disambiguationData":[OSD([sQuery(id+"F6.wireOp",EDGE,"E23.bottom"),subQ0,sQuery(id+"F6.wireOp",EDGE,"E23.left"),sQuery(id+"F6.wireOp",EDGE,"E23.right")])],"isStart":false}),makeQuery(id+"F9.opExtrude","CAP_FACE",FACE,{"disambiguationData":[OSD([sQuery(id+"F8.wireOp",EDGE,"E25.bottom"),sQuery(id+"F8.wireOp",EDGE,"E25.top"),sQuery(id+"F8.wireOp",EDGE,"E25.left"),sQuery(id+"F8.wireOp",EDGE,"E25.right")])],"isStart":false}),makeQuery(id+"F9.opExtrude","CAP_FACE",FACE,{"disambiguationData":[OSD([sQuery(id+"F8.wireOp",EDGE,"E26.bottom"),sQuery(id+"F8.wireOp",EDGE,"E26.top"),sQuery(id+"F8.wireOp",EDGE,"E26.left"),sQuery(id+"F8.wireOp",EDGE,"E26.right")])],"isStart":false})]})],"blendedInto":[makeQuery(id+"F9.boolean.opBoolean","MERGE",FACE,{"derivedFrom":[makeQuery(id+"F7.opExtrude","CAP_FACE",FACE,{"disambiguationData":[OSD([sQuery(id+"F6.wireOp",EDGE,"E22.bottom"),sQuery(id+"F6.wireOp",EDGE,"E22.top"),sQuery(id+"F6.wireOp",EDGE,"E22.left"),sQuery(id+"F6.wireOp",EDGE,"E22.right")])],"isStart":false}),makeQuery(id+"F7.opExtrude","CAP_FACE",FACE,{"disambiguationData":[OSD([sQuery(id+"F6.wireOp",EDGE,"E23.bottom"),subQ0,sQuery(id+"F6.wireOp",EDGE,"E23.left"),sQuery(id+"F6.wireOp",EDGE,"E23.right")])],"isStart":false}),makeQuery(id+"F9.opExtrude","CAP_FACE",FACE,{"disambiguationData":[OSD([sQuery(id+"F8.wireOp",EDGE,"E25.bottom"),sQuery(id+"F8.wireOp",EDGE,"E25.top"),sQuery(id+"F8.wireOp",EDGE,"E25.left"),sQuery(id+"F8.wireOp",EDGE,"E25.right")])],"isStart":false}),makeQuery(id+"F9.opExtrude","CAP_FACE",FACE,{"disambiguationData":[OSD([sQuery(id+"F8.wireOp",EDGE,"E26.bottom"),sQuery(id+"F8.wireOp",EDGE,"E26.top"),sQuery(id+"F8.wireOp",EDGE,"E26.left"),sQuery(id+"F8.wireOp",EDGE,"E26.right")])],"isStart":false})]})]});}
            var Q11;
            {var subQ0=sQuery(id+"F6.wireOp",EDGE,"E22.top");Q11=makeQuery(id+"F11.opChamfer","BLEND_EDGE",EDGE,{"blendedFrom":[makeQuery(id+"F7.opExtrude","CAP_EDGE",EDGE,{"disambiguationData":[OSD([subQ0])],"isStart":false}),makeQuery(id+"F9.boolean.opBoolean","MERGE",FACE,{"derivedFrom":[makeQuery(id+"F7.opExtrude","CAP_FACE",FACE,{"disambiguationData":[OSD([sQuery(id+"F6.wireOp",EDGE,"E22.bottom"),subQ0,sQuery(id+"F6.wireOp",EDGE,"E22.left"),sQuery(id+"F6.wireOp",EDGE,"E22.right")])],"isStart":false}),makeQuery(id+"F7.opExtrude","CAP_FACE",FACE,{"disambiguationData":[OSD([sQuery(id+"F6.wireOp",EDGE,"E23.bottom"),sQuery(id+"F6.wireOp",EDGE,"E23.top"),sQuery(id+"F6.wireOp",EDGE,"E23.left"),sQuery(id+"F6.wireOp",EDGE,"E23.right")])],"isStart":false}),makeQuery(id+"F9.opExtrude","CAP_FACE",FACE,{"disambiguationData":[OSD([sQuery(id+"F8.wireOp",EDGE,"E25.bottom"),sQuery(id+"F8.wireOp",EDGE,"E25.top"),sQuery(id+"F8.wireOp",EDGE,"E25.left"),sQuery(id+"F8.wireOp",EDGE,"E25.right")])],"isStart":false}),makeQuery(id+"F9.opExtrude","CAP_FACE",FACE,{"disambiguationData":[OSD([sQuery(id+"F8.wireOp",EDGE,"E26.bottom"),sQuery(id+"F8.wireOp",EDGE,"E26.top"),sQuery(id+"F8.wireOp",EDGE,"E26.left"),sQuery(id+"F8.wireOp",EDGE,"E26.right")])],"isStart":false})]})],"blendedInto":[makeQuery(id+"F9.boolean.opBoolean","MERGE",FACE,{"derivedFrom":[makeQuery(id+"F7.opExtrude","CAP_FACE",FACE,{"disambiguationData":[OSD([sQuery(id+"F6.wireOp",EDGE,"E22.bottom"),subQ0,sQuery(id+"F6.wireOp",EDGE,"E22.left"),sQuery(id+"F6.wireOp",EDGE,"E22.right")])],"isStart":false}),makeQuery(id+"F7.opExtrude","CAP_FACE",FACE,{"disambiguationData":[OSD([sQuery(id+"F6.wireOp",EDGE,"E23.bottom"),sQuery(id+"F6.wireOp",EDGE,"E23.top"),sQuery(id+"F6.wireOp",EDGE,"E23.left"),sQuery(id+"F6.wireOp",EDGE,"E23.right")])],"isStart":false}),makeQuery(id+"F9.opExtrude","CAP_FACE",FACE,{"disambiguationData":[OSD([sQuery(id+"F8.wireOp",EDGE,"E25.bottom"),sQuery(id+"F8.wireOp",EDGE,"E25.top"),sQuery(id+"F8.wireOp",EDGE,"E25.left"),sQuery(id+"F8.wireOp",EDGE,"E25.right")])],"isStart":false}),makeQuery(id+"F9.opExtrude","CAP_FACE",FACE,{"disambiguationData":[OSD([sQuery(id+"F8.wireOp",EDGE,"E26.bottom"),sQuery(id+"F8.wireOp",EDGE,"E26.top"),sQuery(id+"F8.wireOp",EDGE,"E26.left"),sQuery(id+"F8.wireOp",EDGE,"E26.right")])],"isStart":false})]})]});}
            var Q12;
            {var subQ0=sQuery(id+"F6.wireOp",EDGE,"E22.bottom");Q12=makeQuery(id+"F11.opChamfer","BLEND_EDGE",EDGE,{"blendedFrom":[makeQuery(id+"F7.opExtrude","CAP_EDGE",EDGE,{"disambiguationData":[OSD([subQ0])],"isStart":false}),makeQuery(id+"F9.boolean.opBoolean","MERGE",FACE,{"derivedFrom":[makeQuery(id+"F7.opExtrude","CAP_FACE",FACE,{"disambiguationData":[OSD([subQ0,sQuery(id+"F6.wireOp",EDGE,"E22.top"),sQuery(id+"F6.wireOp",EDGE,"E22.left"),sQuery(id+"F6.wireOp",EDGE,"E22.right")])],"isStart":false}),makeQuery(id+"F7.opExtrude","CAP_FACE",FACE,{"disambiguationData":[OSD([sQuery(id+"F6.wireOp",EDGE,"E23.bottom"),sQuery(id+"F6.wireOp",EDGE,"E23.top"),sQuery(id+"F6.wireOp",EDGE,"E23.left"),sQuery(id+"F6.wireOp",EDGE,"E23.right")])],"isStart":false}),makeQuery(id+"F9.opExtrude","CAP_FACE",FACE,{"disambiguationData":[OSD([sQuery(id+"F8.wireOp",EDGE,"E25.bottom"),sQuery(id+"F8.wireOp",EDGE,"E25.top"),sQuery(id+"F8.wireOp",EDGE,"E25.left"),sQuery(id+"F8.wireOp",EDGE,"E25.right")])],"isStart":false}),makeQuery(id+"F9.opExtrude","CAP_FACE",FACE,{"disambiguationData":[OSD([sQuery(id+"F8.wireOp",EDGE,"E26.bottom"),sQuery(id+"F8.wireOp",EDGE,"E26.top"),sQuery(id+"F8.wireOp",EDGE,"E26.left"),sQuery(id+"F8.wireOp",EDGE,"E26.right")])],"isStart":false})]})],"blendedInto":[makeQuery(id+"F9.boolean.opBoolean","MERGE",FACE,{"derivedFrom":[makeQuery(id+"F7.opExtrude","CAP_FACE",FACE,{"disambiguationData":[OSD([subQ0,sQuery(id+"F6.wireOp",EDGE,"E22.top"),sQuery(id+"F6.wireOp",EDGE,"E22.left"),sQuery(id+"F6.wireOp",EDGE,"E22.right")])],"isStart":false}),makeQuery(id+"F7.opExtrude","CAP_FACE",FACE,{"disambiguationData":[OSD([sQuery(id+"F6.wireOp",EDGE,"E23.bottom"),sQuery(id+"F6.wireOp",EDGE,"E23.top"),sQuery(id+"F6.wireOp",EDGE,"E23.left"),sQuery(id+"F6.wireOp",EDGE,"E23.right")])],"isStart":false}),makeQuery(id+"F9.opExtrude","CAP_FACE",FACE,{"disambiguationData":[OSD([sQuery(id+"F8.wireOp",EDGE,"E25.bottom"),sQuery(id+"F8.wireOp",EDGE,"E25.top"),sQuery(id+"F8.wireOp",EDGE,"E25.left"),sQuery(id+"F8.wireOp",EDGE,"E25.right")])],"isStart":false}),makeQuery(id+"F9.opExtrude","CAP_FACE",FACE,{"disambiguationData":[OSD([sQuery(id+"F8.wireOp",EDGE,"E26.bottom"),sQuery(id+"F8.wireOp",EDGE,"E26.top"),sQuery(id+"F8.wireOp",EDGE,"E26.left"),sQuery(id+"F8.wireOp",EDGE,"E26.right")])],"isStart":false})]})]});}
            var Q13;
            {var subQ0=sQuery(id+"F6.wireOp",EDGE,"E22.bottom");Q13=makeQuery(id+"F11.opChamfer","BLEND_EDGE",EDGE,{"blendedFrom":[makeQuery(id+"F7.opExtrude","CAP_EDGE",EDGE,{"disambiguationData":[OSD([subQ0])],"isStart":false}),makeQuery(id+"F7.boolean.opBoolean","MERGE",FACE,{"derivedFrom":[makeQuery(id+"F1.opExtrude","SWEPT_FACE",FACE,{"disambiguationData":[OSD([sQuery(id+"F0.wireOp",EDGE,"E5.bottom")])]}),makeQuery(id+"F7.opExtrude","SWEPT_FACE",FACE,{"disambiguationData":[OSD([subQ0])]}),makeQuery(id+"F7.opExtrude","SWEPT_FACE",FACE,{"disambiguationData":[OSD([sQuery(id+"F6.wireOp",EDGE,"E23.bottom")])]})]})],"blendedInto":[makeQuery(id+"F7.boolean.opBoolean","MERGE",FACE,{"derivedFrom":[makeQuery(id+"F1.opExtrude","SWEPT_FACE",FACE,{"disambiguationData":[OSD([sQuery(id+"F0.wireOp",EDGE,"E5.bottom")])]}),makeQuery(id+"F7.opExtrude","SWEPT_FACE",FACE,{"disambiguationData":[OSD([subQ0])]}),makeQuery(id+"F7.opExtrude","SWEPT_FACE",FACE,{"disambiguationData":[OSD([sQuery(id+"F6.wireOp",EDGE,"E23.bottom")])]})]})]});}
            var Q14;
            {var subQ0=sQuery(id+"F6.wireOp",EDGE,"E23.bottom");Q14=makeQuery(id+"F11.opChamfer","BLEND_EDGE",EDGE,{"blendedFrom":[makeQuery(id+"F7.opExtrude","CAP_EDGE",EDGE,{"disambiguationData":[OSD([subQ0])],"isStart":false}),makeQuery(id+"F9.boolean.opBoolean","MERGE",FACE,{"derivedFrom":[makeQuery(id+"F7.opExtrude","CAP_FACE",FACE,{"disambiguationData":[OSD([sQuery(id+"F6.wireOp",EDGE,"E22.bottom"),sQuery(id+"F6.wireOp",EDGE,"E22.top"),sQuery(id+"F6.wireOp",EDGE,"E22.left"),sQuery(id+"F6.wireOp",EDGE,"E22.right")])],"isStart":false}),makeQuery(id+"F7.opExtrude","CAP_FACE",FACE,{"disambiguationData":[OSD([subQ0,sQuery(id+"F6.wireOp",EDGE,"E23.top"),sQuery(id+"F6.wireOp",EDGE,"E23.left"),sQuery(id+"F6.wireOp",EDGE,"E23.right")])],"isStart":false}),makeQuery(id+"F9.opExtrude","CAP_FACE",FACE,{"disambiguationData":[OSD([sQuery(id+"F8.wireOp",EDGE,"E25.bottom"),sQuery(id+"F8.wireOp",EDGE,"E25.top"),sQuery(id+"F8.wireOp",EDGE,"E25.left"),sQuery(id+"F8.wireOp",EDGE,"E25.right")])],"isStart":false}),makeQuery(id+"F9.opExtrude","CAP_FACE",FACE,{"disambiguationData":[OSD([sQuery(id+"F8.wireOp",EDGE,"E26.bottom"),sQuery(id+"F8.wireOp",EDGE,"E26.top"),sQuery(id+"F8.wireOp",EDGE,"E26.left"),sQuery(id+"F8.wireOp",EDGE,"E26.right")])],"isStart":false})]})],"blendedInto":[makeQuery(id+"F9.boolean.opBoolean","MERGE",FACE,{"derivedFrom":[makeQuery(id+"F7.opExtrude","CAP_FACE",FACE,{"disambiguationData":[OSD([sQuery(id+"F6.wireOp",EDGE,"E22.bottom"),sQuery(id+"F6.wireOp",EDGE,"E22.top"),sQuery(id+"F6.wireOp",EDGE,"E22.left"),sQuery(id+"F6.wireOp",EDGE,"E22.right")])],"isStart":false}),makeQuery(id+"F7.opExtrude","CAP_FACE",FACE,{"disambiguationData":[OSD([subQ0,sQuery(id+"F6.wireOp",EDGE,"E23.top"),sQuery(id+"F6.wireOp",EDGE,"E23.left"),sQuery(id+"F6.wireOp",EDGE,"E23.right")])],"isStart":false}),makeQuery(id+"F9.opExtrude","CAP_FACE",FACE,{"disambiguationData":[OSD([sQuery(id+"F8.wireOp",EDGE,"E25.bottom"),sQuery(id+"F8.wireOp",EDGE,"E25.top"),sQuery(id+"F8.wireOp",EDGE,"E25.left"),sQuery(id+"F8.wireOp",EDGE,"E25.right")])],"isStart":false}),makeQuery(id+"F9.opExtrude","CAP_FACE",FACE,{"disambiguationData":[OSD([sQuery(id+"F8.wireOp",EDGE,"E26.bottom"),sQuery(id+"F8.wireOp",EDGE,"E26.top"),sQuery(id+"F8.wireOp",EDGE,"E26.left"),sQuery(id+"F8.wireOp",EDGE,"E26.right")])],"isStart":false})]})]});}
            var Q15;
            {var subQ0=sQuery(id+"F6.wireOp",EDGE,"E23.bottom");Q15=makeQuery(id+"F11.opChamfer","BLEND_EDGE",EDGE,{"blendedFrom":[makeQuery(id+"F7.opExtrude","CAP_EDGE",EDGE,{"disambiguationData":[OSD([subQ0])],"isStart":false}),makeQuery(id+"F7.boolean.opBoolean","MERGE",FACE,{"derivedFrom":[makeQuery(id+"F1.opExtrude","SWEPT_FACE",FACE,{"disambiguationData":[OSD([sQuery(id+"F0.wireOp",EDGE,"E5.bottom")])]}),makeQuery(id+"F7.opExtrude","SWEPT_FACE",FACE,{"disambiguationData":[OSD([sQuery(id+"F6.wireOp",EDGE,"E22.bottom")])]}),makeQuery(id+"F7.opExtrude","SWEPT_FACE",FACE,{"disambiguationData":[OSD([subQ0])]})]})],"blendedInto":[makeQuery(id+"F7.boolean.opBoolean","MERGE",FACE,{"derivedFrom":[makeQuery(id+"F1.opExtrude","SWEPT_FACE",FACE,{"disambiguationData":[OSD([sQuery(id+"F0.wireOp",EDGE,"E5.bottom")])]}),makeQuery(id+"F7.opExtrude","SWEPT_FACE",FACE,{"disambiguationData":[OSD([sQuery(id+"F6.wireOp",EDGE,"E22.bottom")])]}),makeQuery(id+"F7.opExtrude","SWEPT_FACE",FACE,{"disambiguationData":[OSD([subQ0])]})]})]});}
            fillet(context, id + "F12", {"entities" : qUnion([Q0, Q1, Q2, Q3, Q4, Q5, Q6, Q7, Q8, Q9, Q10, Q11, Q12, Q13, Q14, Q15]), "radius" : 3.17 * mm, "tangentPropagation" : true, "allowEdgeOverflow" : false});
        }
        {
            var Q0;
            Q0=qCreatedBy(makeId("Front.planeOp"),FACE);
            var sketch = newSketch(context, id + "F13", { "sketchPlane" : qUnion([Q0])});
            skCircle(sketch, "E28", {"center": v(-38.1, 31.75) * mm, "radius": 2.48 * mm});
            skCircle(sketch, "E29", {"center": v(38.1, 31.75) * mm, "radius": 2.48 * mm});
            skLineSegment(sketch, "E30.0", {"start": v(-44.39, 0) * mm, "end": v(-31.81, 0) * mm, "construction": true});
            skLineSegment(sketch, "E31.0", {"start": v(31.81, 0) * mm, "end": v(44.39, 0) * mm, "construction": true});
            skLineSegment(sketch, "E32", {"start": v(-38.1, 31.75) * mm, "end": v(-38.1, 0) * mm, "construction": true});
            skPoint(sketch, "E32.endSnap0", {"position": v(-38.1, 0) * mm});
            skLineSegment(sketch, "E33", {"start": v(38.1, 0) * mm, "end": v(38.1, 31.75) * mm, "construction": true});
            skSolve(sketch);
        }
        {
            var Q0;
            Q0 = qSketchRegion(id + "F13", true);
            extrude(context, id + "F14", {"entities" : qUnion([Q0]), "operationType" : NewBodyOperationType.REMOVE, "oppositeDirection" : true, "depth" : 25.4 * mm, "hasSecondDirection" : true, "secondDirectionOppositeDirection" : false, "secondDirectionDepth" : 25.4 * mm});
        }
    });
